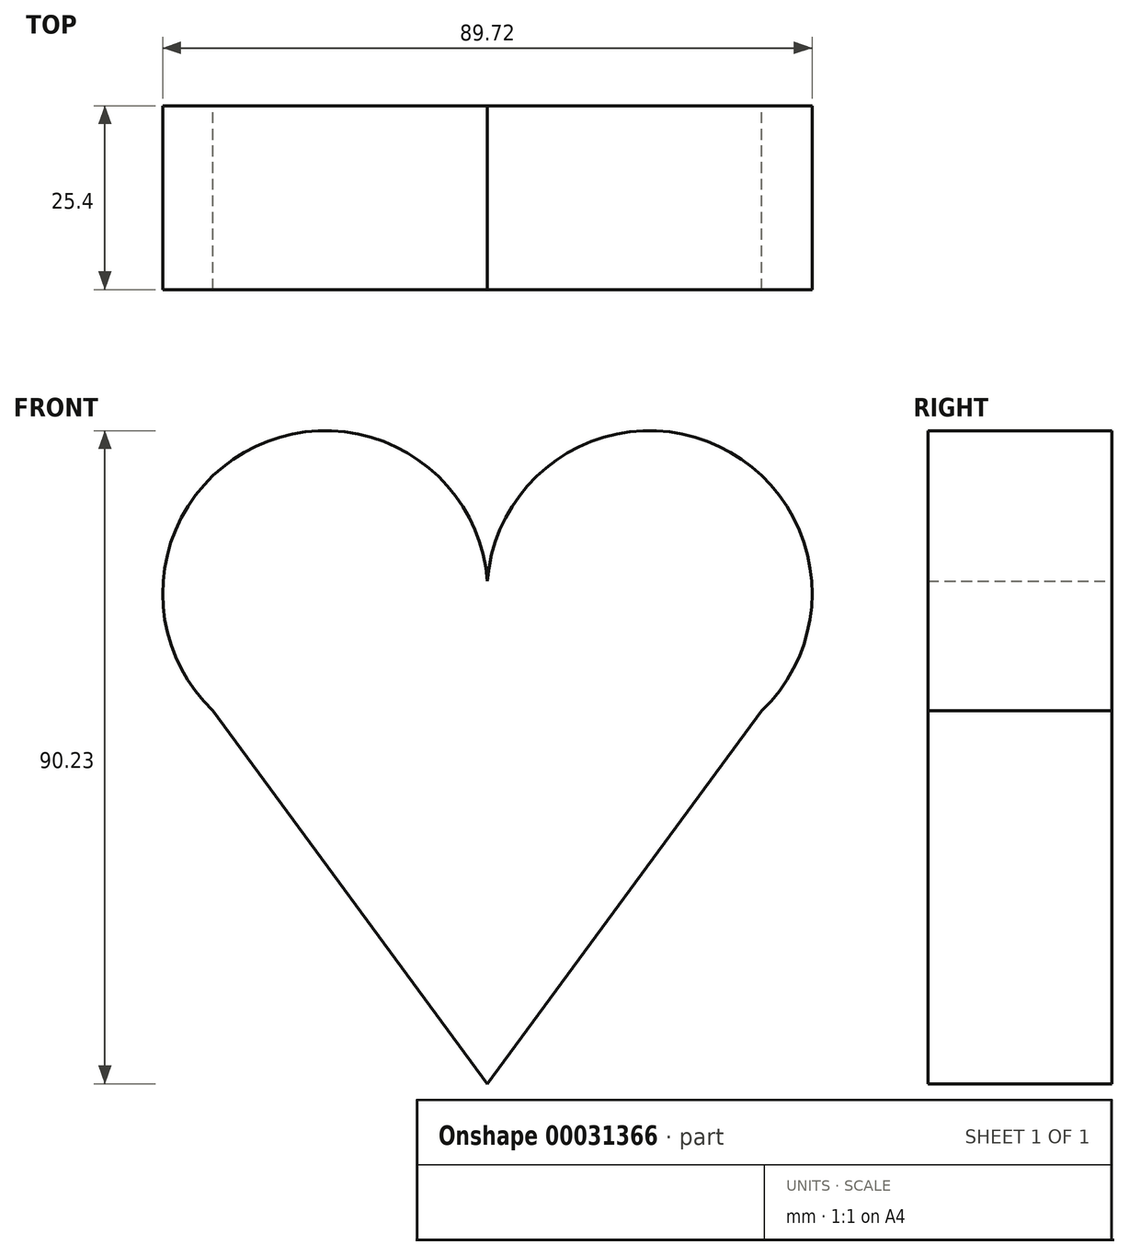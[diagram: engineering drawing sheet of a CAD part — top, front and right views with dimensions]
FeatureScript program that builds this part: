
annotation { "Feature Type Name" : "Feature", "Feature Type Description" : "" }
export const myFeature = defineFeature(function(context is Context, id is Id, definition is map)
    precondition{}
    {
        {
            var Q0;
            Q0=qCreatedBy(makeId("Front.planeOp"),FACE);
            var sketch = newSketch(context, id + "F0", { "sketchPlane" : qUnion([Q0])});
            skArc(sketch, "E0", {"start": v(37.9, 6.43) * mm, "mid": v(32.01, 42.99) * mm, "end": v(0, 24.38) * mm});
            skLineSegment(sketch, "E1", {"start": v(0, -45.08) * mm, "end": v(37.9, 6.43) * mm});
            skArc(sketch, "E2.MirrorCS", {"start": v(-37.9, 6.43) * mm, "mid": v(-32.01, 42.99) * mm, "end": v(0, 24.38) * mm});
            skLineSegment(sketch, "E3.MirrorCS", {"start": v(0, -45.08) * mm, "end": v(-37.9, 6.43) * mm});
            skPoint(sketch, "E4.orphan", {"position": v(0, 20.99) * mm});
            skSolve(sketch);
        }
        {
            var Q0;
            Q0=makeQuery(id+"F0.imprint","IMPRINT",FACE,{"disambiguationData":[TD([[makeQuery(id+"F0.imprint","IMPRINT",EDGE,{"derivedFrom":sQuery(id+"F0.wireOp",EDGE,"E0")}),1.0]])]});
            extrude(context, id + "F1", {"entities" : qUnion([Q0]), "depth" : 25.4 * mm});
        }
    });
